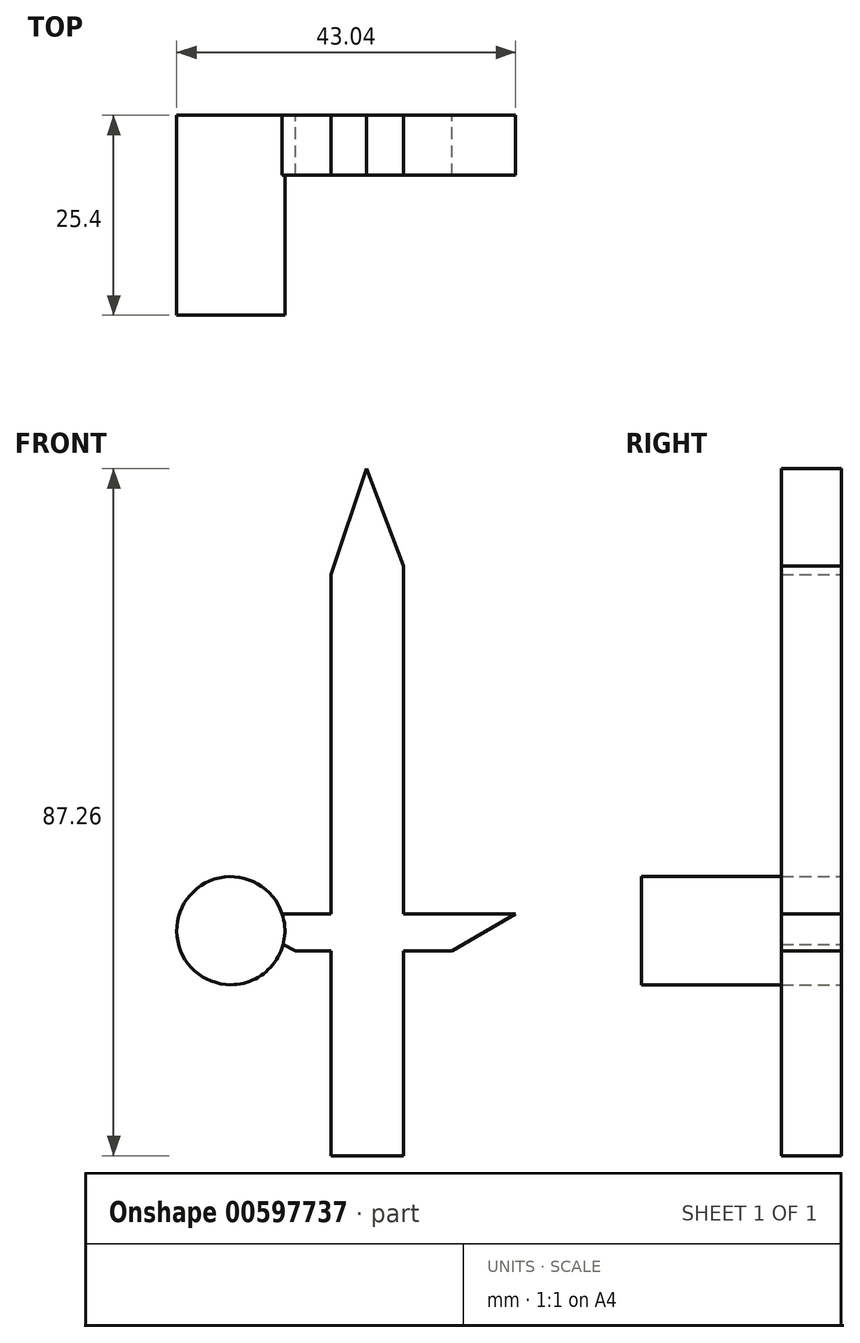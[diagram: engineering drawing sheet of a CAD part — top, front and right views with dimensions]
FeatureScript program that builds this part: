
annotation { "Feature Type Name" : "Feature", "Feature Type Description" : "" }
export const myFeature = defineFeature(function(context is Context, id is Id, definition is map)
    precondition{}
    {
        {
            var Q0;
            Q0=qCreatedBy(makeId("Front.planeOp"),FACE);
            var sketch = newSketch(context, id + "F0", { "sketchPlane" : qUnion([Q0])});
            skLineSegment(sketch, "E0", {"start": v(0, 0) * mm, "end": v(-18.12, 0) * mm});
            skLineSegment(sketch, "E1", {"start": v(-18.12, 0) * mm, "end": v(-9, -4.7) * mm});
            skLineSegment(sketch, "E2", {"start": v(-9, -4.7) * mm, "end": v(0, -4.7) * mm});
            skLineSegment(sketch, "E3", {"start": v(0, -4.7) * mm, "end": v(0, 0) * mm});
            skLineSegment(sketch, "E4", {"start": v(0, 0) * mm, "end": v(10.87, 0) * mm});
            skLineSegment(sketch, "E5", {"start": v(10.87, 0) * mm, "end": v(18.93, 0) * mm});
            skLineSegment(sketch, "E6", {"start": v(18.93, 0) * mm, "end": v(10.87, -4.7) * mm});
            skLineSegment(sketch, "E7", {"start": v(10.87, -4.7) * mm, "end": v(0, -4.7) * mm});
            skLineSegment(sketch, "E8", {"start": v(-4.5, -4.7) * mm, "end": v(-4.5, -30.74) * mm});
            skLineSegment(sketch, "E9", {"start": v(-4.5, -30.74) * mm, "end": v(0, -30.74) * mm});
            skLineSegment(sketch, "E10", {"start": v(0, -30.74) * mm, "end": v(4.7, -30.74) * mm});
            skLineSegment(sketch, "E11", {"start": v(4.7, -30.74) * mm, "end": v(4.7, -4.7) * mm});
            skLineSegment(sketch, "E12", {"start": v(4.7, -4.7) * mm, "end": v(-4.5, -4.7) * mm});
            skLineSegment(sketch, "E13", {"start": v(-4.5, 0) * mm, "end": v(-4.5, 26.45) * mm});
            skLineSegment(sketch, "E14", {"start": v(-4.5, 26.45) * mm, "end": v(-4.5, 43.1) * mm});
            skLineSegment(sketch, "E15", {"start": v(-4.5, 43.1) * mm, "end": v(0, 56.52) * mm});
            skLineSegment(sketch, "E16", {"start": v(0, 56.52) * mm, "end": v(4.7, 44.17) * mm});
            skLineSegment(sketch, "E17", {"start": v(4.7, 44.17) * mm, "end": v(4.7, 0) * mm});
            skFitSpline(sketch, "E18", {"points": [v(-4.5, -24.84) * mm, v(0, -26.18) * mm, v(4.7, -24.3) * mm], "startDerivative": vector(9.15, -4.31) * mm, "endDerivative": vector(9.24, 5.33) * mm});
            skFitSpline(sketch, "E19", {"points": [v(-4.5, -17.72) * mm, v(0, -21.34) * mm, v(4.7, -17.72) * mm], "startDerivative": vector(8.99, -10.9) * mm, "endDerivative": vector(9.4, 10.85) * mm});
            skFitSpline(sketch, "E20", {"points": [v(-4.5, -12.22) * mm, v(0, -14.63) * mm, v(4.7, -12.22) * mm], "startDerivative": vector(9.01, -7.27) * mm, "endDerivative": vector(9.38, 7.23) * mm});
            skFitSpline(sketch, "E21", {"points": [v(-4.5, -7.92) * mm, v(0, -10.07) * mm, v(4.7, -8.73) * mm], "startDerivative": vector(8.83, -6.03) * mm, "endDerivative": vector(9.57, 4.43) * mm});
            skLineSegment(sketch, "E22", {"start": v(-18.12, 0) * mm, "end": v(0, -4.7) * mm});
            skLineSegment(sketch, "E23", {"start": v(4.7, -4.7) * mm, "end": v(18.93, 0) * mm});
            skSolve(sketch);
        }
        {
            var Q0;
            Q0 = qSketchRegion(id + "F0", true);
            extrude(context, id + "F1", {"entities" : qUnion([Q0]), "depth" : 7.62 * mm, "offsetDistance" : 25.4 * mm});
        }
        {
            var Q0;
            Q0=makeQuery(id+"F1.opExtrude","CAP_FACE",FACE,{"disambiguationData":[OSD([sQuery(id+"F0.wireOp",EDGE,"E0"),sQuery(id+"F0.wireOp",EDGE,"E1"),sQuery(id+"F0.wireOp",EDGE,"E2"),sQuery(id+"F0.wireOp",EDGE,"E4"),sQuery(id+"F0.wireOp",EDGE,"E5"),sQuery(id+"F0.wireOp",EDGE,"E6"),sQuery(id+"F0.wireOp",EDGE,"E7"),sQuery(id+"F0.wireOp",EDGE,"E8"),sQuery(id+"F0.wireOp",EDGE,"E9"),sQuery(id+"F0.wireOp",EDGE,"E10"),sQuery(id+"F0.wireOp",EDGE,"E11"),sQuery(id+"F0.wireOp",EDGE,"E13"),sQuery(id+"F0.wireOp",EDGE,"E14"),sQuery(id+"F0.wireOp",EDGE,"E15"),sQuery(id+"F0.wireOp",EDGE,"E16"),sQuery(id+"F0.wireOp",EDGE,"E17")])],"isStart":false});
            extrude(context, id + "F2", {"entities" : qUnion([Q0]), "operationType" : NewBodyOperationType.ADD, "depth" : 25.4 * mm, "offsetDistance" : 25.4 * mm});
        }
        {
            var Q0;
            Q0=makeQuery(id+"F2.opExtrude","CAP_FACE",FACE,{"disambiguationData":[OSD([sQuery(id+"F0.wireOp",EDGE,"E0"),sQuery(id+"F0.wireOp",EDGE,"E1"),sQuery(id+"F0.wireOp",EDGE,"E2"),sQuery(id+"F0.wireOp",EDGE,"E4"),sQuery(id+"F0.wireOp",EDGE,"E5"),sQuery(id+"F0.wireOp",EDGE,"E6"),sQuery(id+"F0.wireOp",EDGE,"E7"),sQuery(id+"F0.wireOp",EDGE,"E8"),sQuery(id+"F0.wireOp",EDGE,"E9"),sQuery(id+"F0.wireOp",EDGE,"E10"),sQuery(id+"F0.wireOp",EDGE,"E11"),sQuery(id+"F0.wireOp",EDGE,"E13"),sQuery(id+"F0.wireOp",EDGE,"E14"),sQuery(id+"F0.wireOp",EDGE,"E15"),sQuery(id+"F0.wireOp",EDGE,"E16"),sQuery(id+"F0.wireOp",EDGE,"E17")])],"isStart":false});
            var sketch = newSketch(context, id + "F3", { "sketchPlane" : qUnion([Q0])});
            skSolve(sketch);
        }
        {
            var Q0;
            Q0=makeQuery(id+"F3.imprint","IMPRINT",FACE,{"disambiguationData":[TD([[makeQuery(id+"F3.imprint","IMPRINT",EDGE,{"derivedFrom":makeQuery(id+"F2.opExtrude","CAP_EDGE",EDGE,{"disambiguationData":[OSD([sQuery(id+"F0.wireOp",EDGE,"E0")])],"isStart":false})}),1.0]])]});
            extrude(context, id + "F4", {"entities" : qUnion([Q0]), "operationType" : NewBodyOperationType.REMOVE, "oppositeDirection" : true, "depth" : 25.4 * mm, "offsetDistance" : 25.4 * mm});
        }
        {
            var Q0;
            Q0=qCreatedBy(makeId("Front.planeOp"),FACE);
            var sketch = newSketch(context, id + "F5", { "sketchPlane" : qUnion([Q0])});
            skArc(sketch, "E24", {"start": v(-23.76, 0) * mm, "mid": v(-13.09, -7.62) * mm, "end": v(-17.59, 4.7) * mm});
            skArc(sketch, "E25", {"start": v(-10.87, 0.4) * mm, "mid": v(-17.46, 4.7) * mm, "end": v(-23.76, 0) * mm});
            skSolve(sketch);
        }
        {
            var Q0;
            Q0 = qSketchRegion(id + "F5", true);
            extrude(context, id + "F6", {"entities" : qUnion([Q0]), "operationType" : NewBodyOperationType.ADD, "depth" : 25.4 * mm, "offsetDistance" : 25.4 * mm});
        }
    });
